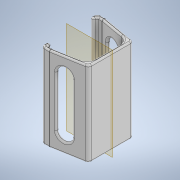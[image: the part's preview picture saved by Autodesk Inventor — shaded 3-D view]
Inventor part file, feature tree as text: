
AUTODESK INVENTOR PART (.ipt)
format: ipt  version: 2020 (Build 240168000, 168)  size: 372,224 bytes
history: native  units: in
note: dims shown in document units (in); Inventor stores cm internally (conversion verified against a paired STEP export)
features: fillet x5, extrude x2, sketch x2, plane x1
ambient origin geometry x8: Origin, YZ Plane, XZ Plane, XY Plane, X Axis, Y Axis, Z Axis, Center Point
bodies: Solid1 (feature_tree)
feature tree (10):
  extrude  "Extrusion1"  Depth=0.7087in
  fillet  "Fillet1"  Radius=0.0687in
  fillet  "Fillet2"  Radius=0.7087in
  fillet  "Fillet3"  Radius=0.0687in
  fillet  "Fillet4"  Radius=0.1969in
  plane  "Work Plane1"
  extrude  "Extrusion2"  Depth=0.0394in
  fillet  "Fillet5"  Radius=0.0787in
  sketch  "Sketch1"  dims[d0=0.9055in d1=0.7087in d2=0.0687in d3=0.7087in d4=0.0687in d5=0.1969in]
  sketch  "Sketch2"  dims[d6=0.1969in d7=0.0787in d8=0.0787in d9=0.0787in d10=0.0787in d11=0.0787in d12=0.0787in d13=0.0787in d14=0.0787in d15=0.0787in d16=0.0787in d17=0.0787in d18=0.0787in d19=1.9685in d20=0.0in d21=0.0787in d22=0.1969in d23=0.0394in d24=0.0354in d25=-0.4375in d26=0.5906in d27=1.1811in d28=0.315in d29=0.315in d30=1.9685in d31=0.0in d32=0.0394in]
